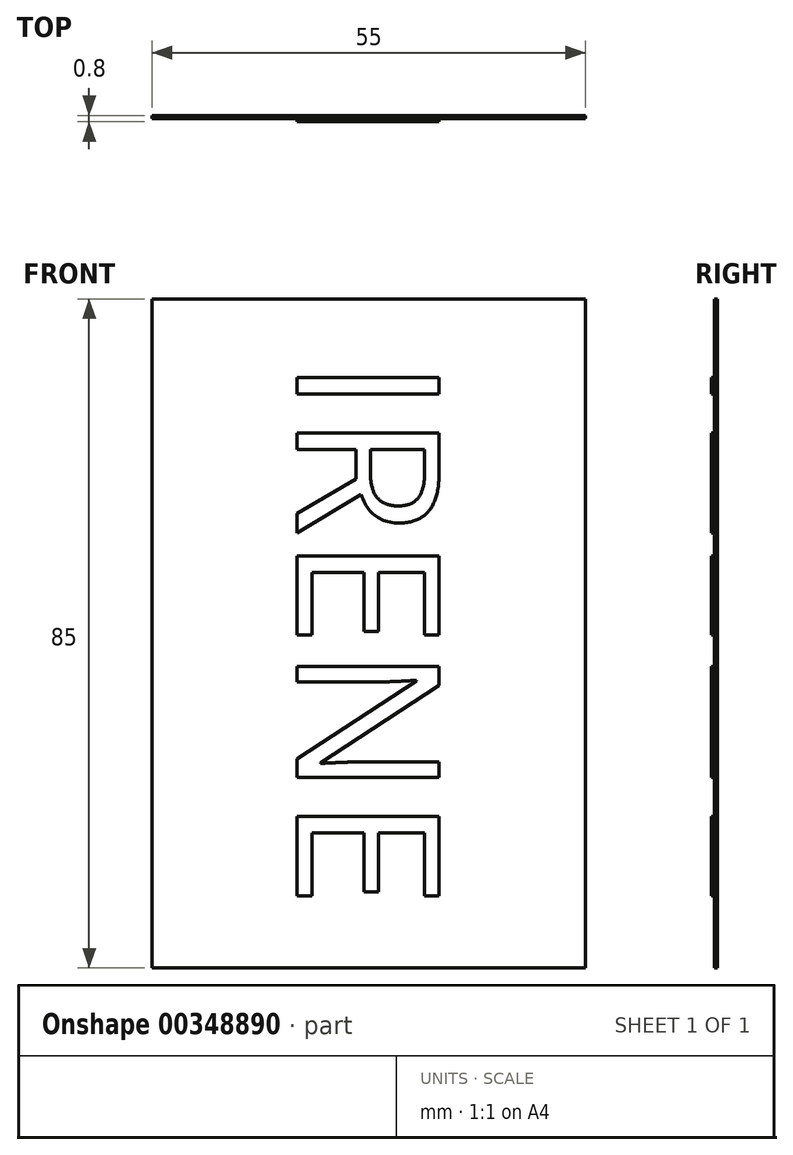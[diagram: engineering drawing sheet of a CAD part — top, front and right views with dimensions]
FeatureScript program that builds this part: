
annotation { "Feature Type Name" : "Feature", "Feature Type Description" : "" }
export const myFeature = defineFeature(function(context is Context, id is Id, definition is map)
    precondition{}
    {
        {
            var Q0;
            Q0=qCreatedBy(makeId("Front.planeOp"),FACE);
            var sketch = newSketch(context, id + "F0", { "sketchPlane" : qUnion([Q0])});
            skLineSegment(sketch, "E0.bottom", {"start": v(-27.5, -42.5) * mm, "end": v(27.5, -42.5) * mm});
            skLineSegment(sketch, "E0.top", {"start": v(-27.5, 42.5) * mm, "end": v(27.5, 42.5) * mm});
            skLineSegment(sketch, "E0.left", {"start": v(-27.5, -42.5) * mm, "end": v(-27.5, 42.5) * mm});
            skLineSegment(sketch, "E0.right", {"start": v(27.5, -42.5) * mm, "end": v(27.5, 42.5) * mm});
            skPoint(sketch, "E0.middle", {"position": v(0, 0) * mm});
            skSolve(sketch);
        }
        {
            var Q0;
            Q0 = qSketchRegion(id + "F0", true);
            extrude(context, id + "F1", {"entities" : qUnion([Q0]), "depth" : 0.4 * mm});
        }
        {
            var Q0;
            Q0=makeQuery(id+"F1.opExtrude","CAP_FACE",FACE,{"disambiguationData":[OSD([sQuery(id+"F0.wireOp",EDGE,"E0.bottom"),sQuery(id+"F0.wireOp",EDGE,"E0.top"),sQuery(id+"F0.wireOp",EDGE,"E0.left"),sQuery(id+"F0.wireOp",EDGE,"E0.right")])],"isStart":false});
            var sketch = newSketch(context, id + "F2", { "sketchPlane" : qUnion([Q0])});
            skText(sketch, "E1", { "text": "IRENE", "fontName": "OpenSans-Regular.ttf"});
            const initialGuessF2  = {"E1": [-0.0091, 0.035, 0, -1, 0.0182]};
            skSetInitialGuess(sketch, initialGuessF2);
            skSolve(sketch);
        }
        {
            var Q0;
            Q0 = qSketchRegion(id + "F2", true);
            extrude(context, id + "F3", {"entities" : qUnion([Q0]), "operationType" : NewBodyOperationType.ADD, "depth" : 0.4 * mm});
        }
    });
